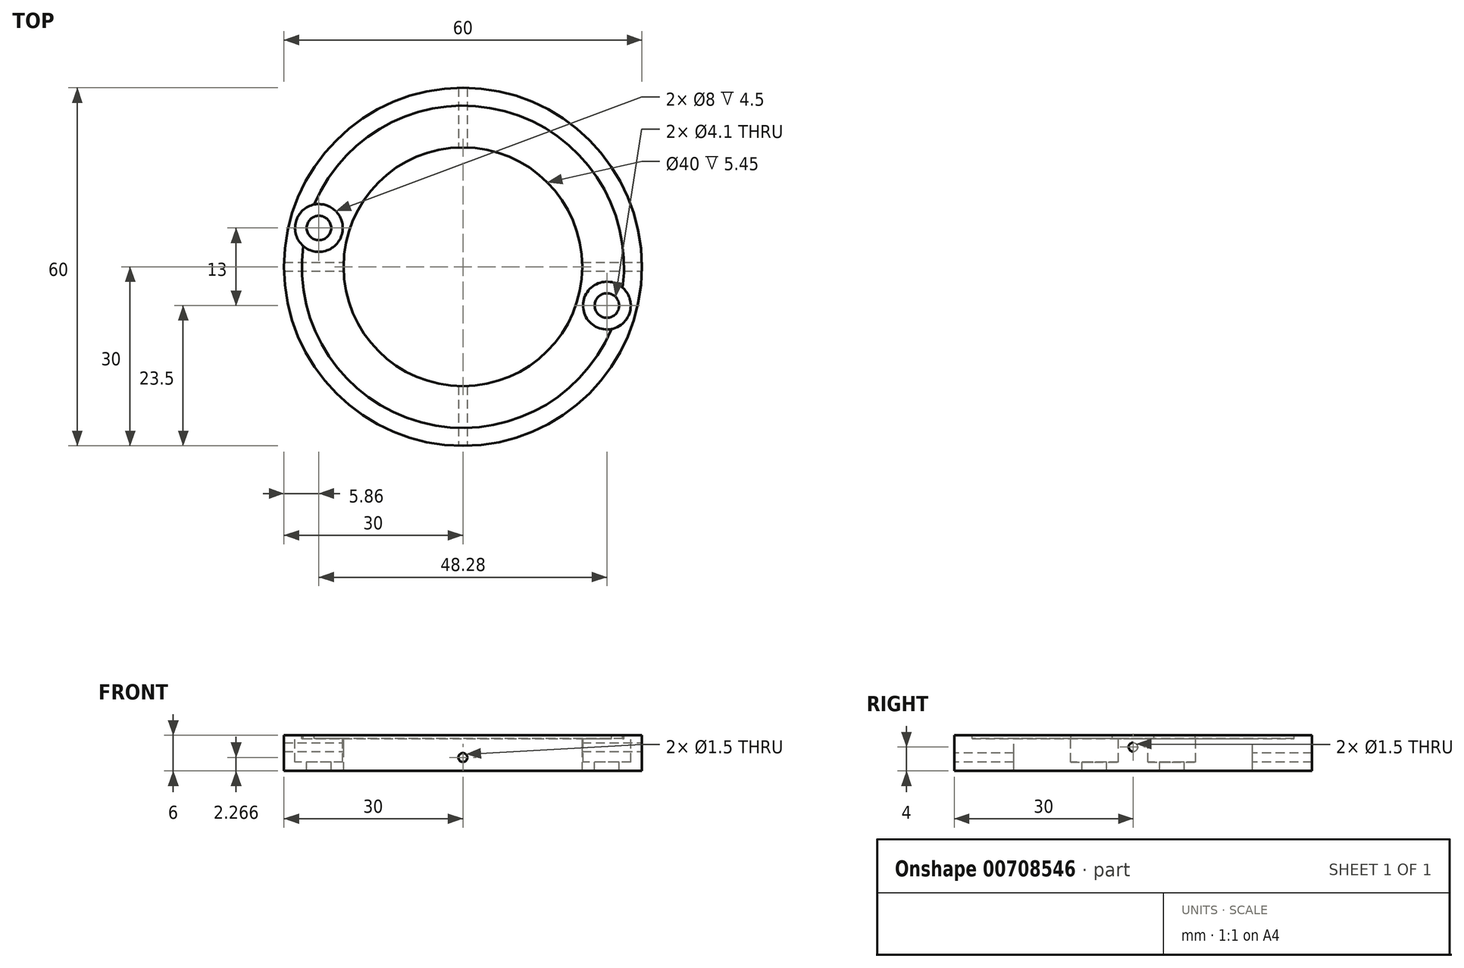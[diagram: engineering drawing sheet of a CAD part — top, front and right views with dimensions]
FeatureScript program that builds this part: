
annotation { "Feature Type Name" : "Feature", "Feature Type Description" : "" }
export const myFeature = defineFeature(function(context is Context, id is Id, definition is map)
    precondition{}
    {
        {
            var Q0;
            Q0=qCreatedBy(makeId("Top.planeOp"),FACE);
            var sketch = newSketch(context, id + "F0", { "sketchPlane" : qUnion([Q0])});
            skCircle(sketch, "E0", {"center": v(0, 0) * mm, "radius": 30 * mm});
            skSolve(sketch);
        }
        {
            var Q0;
            Q0=makeQuery(id+"F0.imprint","IMPRINT",FACE,{"disambiguationData":[TD([[makeQuery(id+"F0.imprint","IMPRINT",EDGE,{"derivedFrom":sQuery(id+"F0.wireOp",EDGE,"E0")}),1.0]])]});
            extrude(context, id + "F1", {"entities" : qUnion([Q0]), "depth" : 6 * mm, "offsetDistance" : 25 * mm});
        }
        {
            var Q0;
            Q0=makeQuery(id+"F1.opExtrude","CAP_FACE",FACE,{"disambiguationData":[OSD([sQuery(id+"F0.wireOp",EDGE,"E0")])],"isStart":false});
            var sketch = newSketch(context, id + "F2", { "sketchPlane" : qUnion([Q0])});
            skCircle(sketch, "E1", {"center": v(0, 0) * mm, "radius": 27 * mm});
            skSolve(sketch);
        }
        {
            var Q0;
            Q0=makeQuery(id+"F2.imprint","IMPRINT",FACE,{"disambiguationData":[TD([[makeQuery(id+"F2.imprint","IMPRINT",EDGE,{"derivedFrom":sQuery(id+"F2.wireOp",EDGE,"E1")}),1.0]])]});
            extrude(context, id + "F3", {"entities" : qUnion([Q0]), "operationType" : NewBodyOperationType.REMOVE, "oppositeDirection" : true, "depth" : 0.55 * mm, "offsetDistance" : 25 * mm});
        }
        {
            var Q0;
            Q0=qCreatedBy(makeId("Front.planeOp"),FACE);
            var sketch = newSketch(context, id + "F4", { "sketchPlane" : qUnion([Q0])});
            skCircle(sketch, "E2", {"center": v(0, 2.27) * mm, "radius": 0.75 * mm});
            skSolve(sketch);
        }
        {
            var Q0;
            Q0 = qSketchRegion(id + "F4", true);
            extrude(context, id + "F5", {"entities" : qUnion([Q0]), "operationType" : NewBodyOperationType.REMOVE, "endBound" : BoundingType.THROUGH_ALL, "oppositeDirection" : true, "depth" : 25 * mm, "offsetDistance" : 25 * mm, "hasSecondDirection" : true, "secondDirectionBound" : SecondDirectionBoundingType.THROUGH_ALL, "secondDirectionOppositeDirection" : false, "secondDirectionDepth" : 25 * mm});
        }
        {
            var Q0;
            Q0=makeQuery(id+"F3.boolean.opBoolean","COPY",FACE,{"derivedFrom":makeQuery(id+"F3.opExtrude","CAP_FACE",FACE,{"disambiguationData":[OSD([sQuery(id+"F2.wireOp",EDGE,"E1")])],"isStart":false})});
            var sketch = newSketch(context, id + "F6", { "sketchPlane" : qUnion([Q0])});
            skCircle(sketch, "E3", {"center": v(0, 0) * mm, "radius": 20 * mm});
            skSolve(sketch);
        }
        {
            var Q0;
            Q0=makeQuery(id+"F6.imprint","IMPRINT",FACE,{"disambiguationData":[TD([[makeQuery(id+"F6.imprint","IMPRINT",EDGE,{"derivedFrom":sQuery(id+"F6.wireOp",EDGE,"E3")}),1.0]])]});
            extrude(context, id + "F7", {"entities" : qUnion([Q0]), "operationType" : NewBodyOperationType.REMOVE, "endBound" : BoundingType.THROUGH_ALL, "oppositeDirection" : true, "depth" : 25 * mm, "offsetDistance" : 25 * mm});
        }
        {
            var Q0;
            Q0=qCreatedBy(makeId("Right.planeOp"),FACE);
            var sketch = newSketch(context, id + "F8", { "sketchPlane" : qUnion([Q0])});
            skCircle(sketch, "E4", {"center": v(0, 4) * mm, "radius": 0.75 * mm});
            skSolve(sketch);
        }
        {
            var Q0;
            Q0 = qSketchRegion(id + "F8", true);
            extrude(context, id + "F9", {"entities" : qUnion([Q0]), "operationType" : NewBodyOperationType.REMOVE, "endBound" : BoundingType.THROUGH_ALL, "oppositeDirection" : true, "depth" : 25 * mm, "offsetDistance" : 25 * mm, "hasSecondDirection" : true, "secondDirectionBound" : SecondDirectionBoundingType.THROUGH_ALL, "secondDirectionOppositeDirection" : false, "secondDirectionDepth" : 25 * mm});
        }
        {
            var Q0;
            Q0=makeQuery(id+"F3.boolean.opBoolean","COPY",FACE,{"derivedFrom":makeQuery(id+"F3.opExtrude","CAP_FACE",FACE,{"disambiguationData":[OSD([sQuery(id+"F2.wireOp",EDGE,"E1")])],"isStart":false})});
            var sketch = newSketch(context, id + "F10", { "sketchPlane" : qUnion([Q0])});
            skCircle(sketch, "E5", {"center": v(24.14, -6.5) * mm, "radius": 4 * mm});
            skCircle(sketch, "E6", {"center": v(-24.14, 6.5) * mm, "radius": 4 * mm});
            skSolve(sketch);
        }
        {
            var Q0;
            {var subQ0=sQuery(id+"F10.wireOp",EDGE,"E6");var subQ1=makeQuery(id+"F3.boolean.opBoolean","COPY",EDGE,{"derivedFrom":makeQuery(id+"F3.opExtrude","CAP_EDGE",EDGE,{"disambiguationData":[OSD([sQuery(id+"F2.wireOp",EDGE,"E1")])],"isStart":false})});var subQ2=makeQuery(id+"F10.imprint","INTERSECT",VERTEX,{"disambiguationData":[OD(0.0)],"derivedFrom":[subQ1,subQ0]});Q0=makeQuery(id+"F10.imprint","IMPRINT",FACE,{"disambiguationData":[TD([[makeQuery(id+"F10.imprint","IMPRINT",EDGE,{"disambiguationData":[TD([[subQ2,-1.0]])],"derivedFrom":subQ0}),1.0]])]});}
            var Q1;
            {var subQ0=sQuery(id+"F10.wireOp",EDGE,"E5");var subQ1=makeQuery(id+"F3.boolean.opBoolean","COPY",EDGE,{"derivedFrom":makeQuery(id+"F3.opExtrude","CAP_EDGE",EDGE,{"disambiguationData":[OSD([sQuery(id+"F2.wireOp",EDGE,"E1")])],"isStart":false})});var subQ2=makeQuery(id+"F10.imprint","INTERSECT",VERTEX,{"disambiguationData":[OD(0.0)],"derivedFrom":[subQ1,subQ0]});Q1=makeQuery(id+"F10.imprint","IMPRINT",FACE,{"disambiguationData":[TD([[makeQuery(id+"F10.imprint","IMPRINT",EDGE,{"disambiguationData":[TD([[subQ2,1.0]])],"derivedFrom":subQ0}),1.0]])]});}
            extrude(context, id + "F11", {"entities" : qUnion([Q0, Q1]), "operationType" : NewBodyOperationType.REMOVE, "oppositeDirection" : true, "depth" : 3.95 * mm, "offsetDistance" : 25 * mm, "hasSecondDirection" : true, "secondDirectionBound" : SecondDirectionBoundingType.THROUGH_ALL, "secondDirectionOppositeDirection" : false, "secondDirectionDepth" : 25 * mm});
        }
        {
            var Q0;
            Q0=makeQuery(id+"F1.opExtrude","CAP_FACE",FACE,{"disambiguationData":[OSD([sQuery(id+"F0.wireOp",EDGE,"E0")])],"isStart":false});
            var sketch = newSketch(context, id + "F12", { "sketchPlane" : qUnion([Q0])});
            skCircle(sketch, "E7", {"center": v(-24.14, 6.5) * mm, "radius": 4 * mm});
            skCircle(sketch, "E8", {"center": v(24.14, -6.5) * mm, "radius": 4 * mm});
            skSolve(sketch);
        }
        {
            var Q0;
            {var subQ0=sQuery(id+"F12.wireOp",EDGE,"E7");var subQ1=sQuery(id+"F10.wireOp",EDGE,"E6");var subQ2=sQuery(id+"F2.wireOp",EDGE,"E1");var subQ3=makeQuery(id+"F3.boolean.opBoolean","COPY",EDGE,{"derivedFrom":makeQuery(id+"F3.opExtrude","CAP_EDGE",EDGE,{"disambiguationData":[OSD([subQ2])],"isStart":false})});var subQ4=sQuery(id+"F10.wireOp",EDGE,"E5");var subQ5=makeQuery(id+"F11.boolean.opBoolean","INTERSECT",EDGE,{"derivedFrom":[makeQuery(id+"F11.opExtrude","SWEPT_FACE",FACE,{"disambiguationData":[OSD([subQ2]),TDD([makeQuery(id+"F10.imprint","IMPRINT",EDGE,{"disambiguationData":[TD([[makeQuery(id+"F10.imprint","INTERSECT",VERTEX,{"disambiguationData":[OD(0.0)],"derivedFrom":[subQ3,subQ4]}),-1.0]])],"derivedFrom":subQ3})])]}),makeQuery(id+"F11.opExtrude","SWEPT_FACE",FACE,{"disambiguationData":[OSD([subQ2]),TDD([makeQuery(id+"F10.imprint","IMPRINT",EDGE,{"disambiguationData":[TD([[makeQuery(id+"F10.imprint","INTERSECT",VERTEX,{"disambiguationData":[OD(0.0)],"derivedFrom":[subQ3,subQ1]}),1.0]])],"derivedFrom":subQ3})])]})]});var subQ6=makeQuery(id+"F12.imprint","INTERSECT",VERTEX,{"disambiguationData":[OD(0.0)],"derivedFrom":[subQ5,subQ0]});Q0=makeQuery(id+"F12.imprint","IMPRINT",FACE,{"disambiguationData":[TD([[makeQuery(id+"F12.imprint","IMPRINT",EDGE,{"disambiguationData":[TD([[subQ6,1.0]])],"derivedFrom":subQ0}),1.0]])]});}
            var Q1;
            {var subQ0=sQuery(id+"F12.wireOp",EDGE,"E8");var subQ1=sQuery(id+"F10.wireOp",EDGE,"E6");var subQ2=sQuery(id+"F2.wireOp",EDGE,"E1");var subQ3=makeQuery(id+"F3.boolean.opBoolean","COPY",EDGE,{"derivedFrom":makeQuery(id+"F3.opExtrude","CAP_EDGE",EDGE,{"disambiguationData":[OSD([subQ2])],"isStart":false})});var subQ4=sQuery(id+"F10.wireOp",EDGE,"E5");var subQ5=makeQuery(id+"F11.boolean.opBoolean","INTERSECT",EDGE,{"derivedFrom":[makeQuery(id+"F11.opExtrude","SWEPT_FACE",FACE,{"disambiguationData":[OSD([subQ2]),TDD([makeQuery(id+"F10.imprint","IMPRINT",EDGE,{"disambiguationData":[TD([[makeQuery(id+"F10.imprint","INTERSECT",VERTEX,{"disambiguationData":[OD(0.0)],"derivedFrom":[subQ3,subQ4]}),-1.0]])],"derivedFrom":subQ3})])]}),makeQuery(id+"F11.opExtrude","SWEPT_FACE",FACE,{"disambiguationData":[OSD([subQ2]),TDD([makeQuery(id+"F10.imprint","IMPRINT",EDGE,{"disambiguationData":[TD([[makeQuery(id+"F10.imprint","INTERSECT",VERTEX,{"disambiguationData":[OD(0.0)],"derivedFrom":[subQ3,subQ1]}),1.0]])],"derivedFrom":subQ3})])]})]});var subQ6=makeQuery(id+"F12.imprint","INTERSECT",VERTEX,{"disambiguationData":[OD(0.0)],"derivedFrom":[subQ5,subQ0]});Q1=makeQuery(id+"F12.imprint","IMPRINT",FACE,{"disambiguationData":[TD([[makeQuery(id+"F12.imprint","IMPRINT",EDGE,{"disambiguationData":[TD([[subQ6,-1.0]])],"derivedFrom":subQ0}),1.0]])]});}
            extrude(context, id + "F13", {"entities" : qUnion([Q0, Q1]), "operationType" : NewBodyOperationType.REMOVE, "oppositeDirection" : true, "depth" : 4.5 * mm, "offsetDistance" : 25 * mm});
        }
        {
            var Q0;
            {var subQ0=sQuery(id+"F2.wireOp",EDGE,"E1");Q0=makeQuery(id+"F13.boolean.opBoolean","MERGE",FACE,{"derivedFrom":[makeQuery(id+"F11.boolean.opBoolean","COPY",FACE,{"derivedFrom":makeQuery(id+"F11.opExtrude","CAP_FACE",FACE,{"disambiguationData":[OSD([subQ0,sQuery(id+"F10.wireOp",EDGE,"E6")])],"isStart":false})}),makeQuery(id+"F13.opExtrude","CAP_FACE",FACE,{"disambiguationData":[OSD([subQ0,sQuery(id+"F12.wireOp",EDGE,"E7")])],"isStart":false})]});}
            var sketch = newSketch(context, id + "F14", { "sketchPlane" : qUnion([Q0])});
            skCircle(sketch, "E9", {"center": v(-24.14, 6.5) * mm, "radius": 2.05 * mm});
            skCircle(sketch, "E10", {"center": v(24.14, -6.5) * mm, "radius": 2.05 * mm});
            skSolve(sketch);
        }
        {
            var Q0;
            Q0=makeQuery(id+"F14.imprint","IMPRINT",FACE,{"disambiguationData":[TD([[makeQuery(id+"F14.imprint","IMPRINT",EDGE,{"derivedFrom":sQuery(id+"F14.wireOp",EDGE,"E9")}),1.0]])]});
            var Q1;
            Q1=makeQuery(id+"F14.imprint","IMPRINT",FACE,{"disambiguationData":[TD([[makeQuery(id+"F14.imprint","IMPRINT",EDGE,{"derivedFrom":sQuery(id+"F14.wireOp",EDGE,"E10")}),1.0]])]});
            extrude(context, id + "F15", {"entities" : qUnion([Q0, Q1]), "operationType" : NewBodyOperationType.REMOVE, "endBound" : BoundingType.THROUGH_ALL, "oppositeDirection" : true, "depth" : 25 * mm, "offsetDistance" : 25 * mm});
        }
    });
